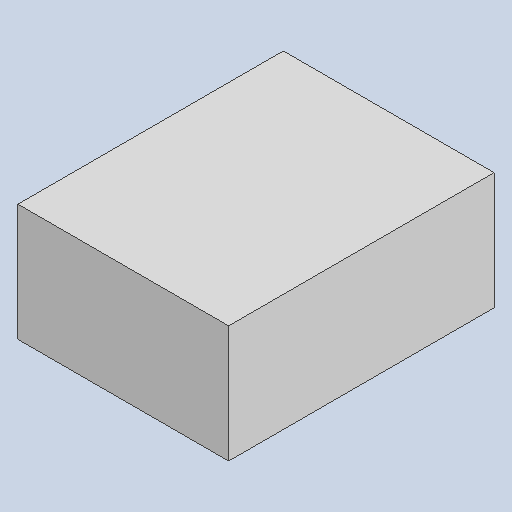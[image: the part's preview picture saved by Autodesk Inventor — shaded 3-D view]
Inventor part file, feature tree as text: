
AUTODESK INVENTOR PART (.ipt)
format: ipt  version: 2022.3 (Build 263350000, 350)  size: 80,896 bytes
history: native  units: mm
features: other x3, sketch x1
ambient origin geometry x8: Origin, YZ Plane, XZ Plane, XY Plane, X Axis, Y Axis, Z Axis, Center Point
bodies: Solid1 (feature_tree)
feature tree (4):
  other  "ktir.ipt"
  other  "Solid1::ktir.ipt"
  other  "TaggingFeature1"
  sketch  "Sketch1"  dims[d0=10.0mm]
